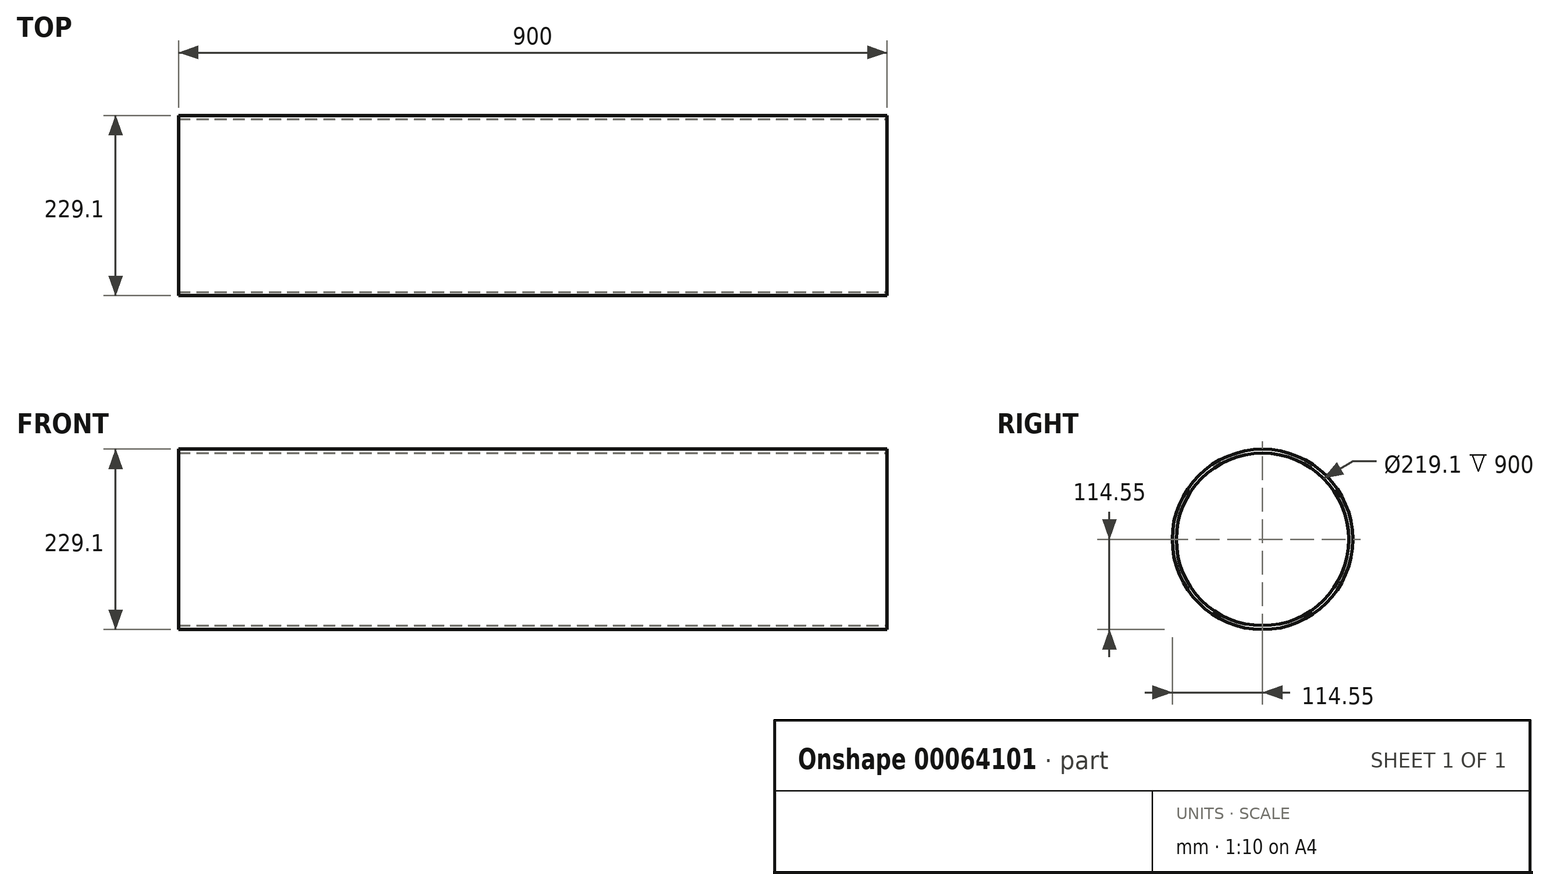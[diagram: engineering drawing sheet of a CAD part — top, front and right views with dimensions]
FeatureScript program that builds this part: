
annotation { "Feature Type Name" : "Feature", "Feature Type Description" : "" }
export const myFeature = defineFeature(function(context is Context, id is Id, definition is map)
    precondition{}
    {
        {
            var Q0;
            Q0=qCreatedBy(makeId("Right.planeOp"),FACE);
            var sketch = newSketch(context, id + "F0", { "sketchPlane" : qUnion([Q0])});
            skCircle(sketch, "E0", {"center": v(0, 0) * mm, "radius": 109.55 * mm});
            skCircle(sketch, "E1", {"center": v(0, 0) * mm, "radius": 114.55 * mm});
            skSolve(sketch);
        }
        {
            var Q0;
            Q0=makeQuery(id+"F0.imprint","IMPRINT",FACE,{"disambiguationData":[TD([[makeQuery(id+"F0.imprint","IMPRINT",EDGE,{"derivedFrom":sQuery(id+"F0.wireOp",EDGE,"E0")}),-1.0]])]});
            extrude(context, id + "F1", {"entities" : qUnion([Q0]), "oppositeDirection" : true, "depth" : 900 * mm});
        }
    });
